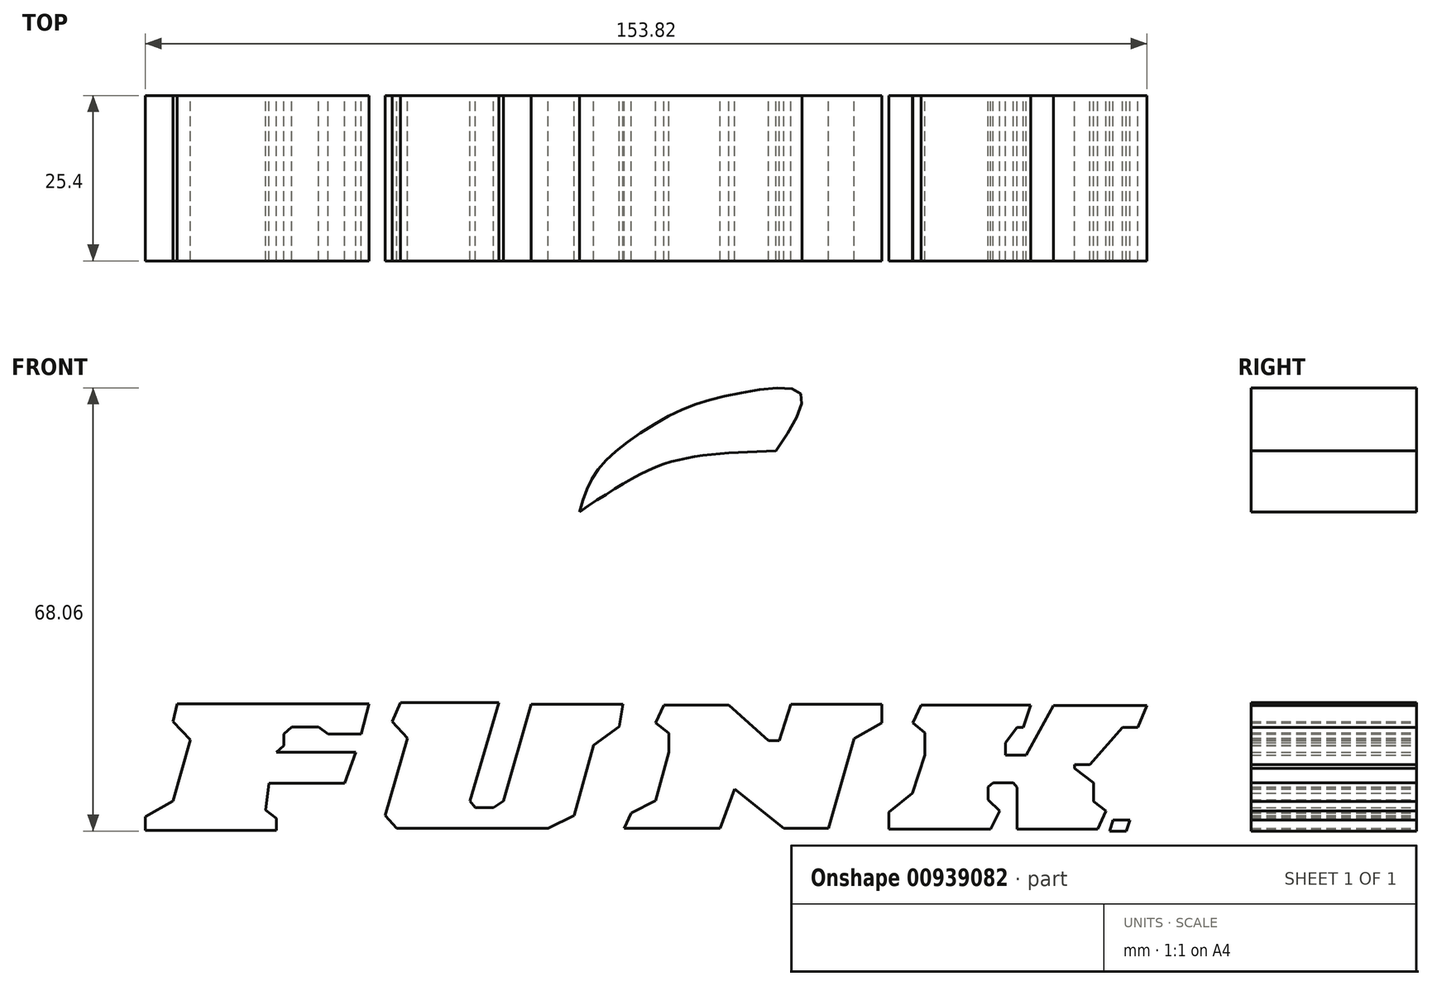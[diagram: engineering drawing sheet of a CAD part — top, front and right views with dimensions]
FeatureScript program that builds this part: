
annotation { "Feature Type Name" : "Feature", "Feature Type Description" : "" }
export const myFeature = defineFeature(function(context is Context, id is Id, definition is map)
    precondition{}
    {
        {
            var Q0;
            Q0=qCreatedBy(makeId("Front.planeOp"),FACE);
            var sketch = newSketch(context, id + "F0", { "sketchPlane" : qUnion([Q0])});
            skLineSegment(sketch, "E0", {"start": v(-70.91, 28.57) * mm, "end": v(-71.55, 25.87) * mm});
            skLineSegment(sketch, "E1", {"start": v(-71.55, 25.87) * mm, "end": v(-68.85, 23.1) * mm});
            skLineSegment(sketch, "E2", {"start": v(-68.85, 23.1) * mm, "end": v(-71.55, 13.7) * mm});
            skLineSegment(sketch, "E3", {"start": v(-71.55, 13.7) * mm, "end": v(-75.78, 11.28) * mm});
            skLineSegment(sketch, "E4", {"start": v(-75.78, 11.28) * mm, "end": v(-75.78, 9.14) * mm});
            skLineSegment(sketch, "E5", {"start": v(-75.78, 9.14) * mm, "end": v(-55.68, 9.14) * mm});
            skLineSegment(sketch, "E6", {"start": v(-55.68, 9.14) * mm, "end": v(-55.68, 11) * mm});
            skLineSegment(sketch, "E7", {"start": v(-55.68, 11) * mm, "end": v(-57.32, 12.28) * mm});
            skLineSegment(sketch, "E8", {"start": v(-57.32, 12.28) * mm, "end": v(-56.82, 16.4) * mm});
            skLineSegment(sketch, "E9", {"start": v(-56.82, 16.4) * mm, "end": v(-45.15, 16.4) * mm});
            skLineSegment(sketch, "E10", {"start": v(-45.15, 16.4) * mm, "end": v(-43.44, 21.17) * mm});
            skLineSegment(sketch, "E11", {"start": v(-43.44, 21.17) * mm, "end": v(-55.68, 21.17) * mm});
            skLineSegment(sketch, "E12", {"start": v(-55.68, 21.17) * mm, "end": v(-54.54, 22.17) * mm});
            skLineSegment(sketch, "E13", {"start": v(-54.54, 22.17) * mm, "end": v(-54.54, 23.95) * mm});
            skLineSegment(sketch, "E14", {"start": v(-54.54, 23.95) * mm, "end": v(-53.33, 25.01) * mm});
            skLineSegment(sketch, "E15", {"start": v(-53.33, 25.01) * mm, "end": v(-49.2, 25.01) * mm});
            skLineSegment(sketch, "E16", {"start": v(-49.2, 25.01) * mm, "end": v(-47.71, 23.95) * mm});
            skLineSegment(sketch, "E17", {"start": v(-47.71, 23.95) * mm, "end": v(-42.66, 23.95) * mm});
            skLineSegment(sketch, "E18", {"start": v(-42.66, 23.95) * mm, "end": v(-41.45, 28.57) * mm});
            skLineSegment(sketch, "E19", {"start": v(-41.45, 28.57) * mm, "end": v(-70.91, 28.57) * mm});
            skLineSegment(sketch, "E20", {"start": v(-36.61, 28.79) * mm, "end": v(-37.9, 25.87) * mm});
            skLineSegment(sketch, "E21", {"start": v(-37.9, 25.87) * mm, "end": v(-35.54, 23.3) * mm});
            skLineSegment(sketch, "E22", {"start": v(-35.54, 23.3) * mm, "end": v(-38.96, 11.42) * mm});
            skLineSegment(sketch, "E23", {"start": v(-38.96, 11.42) * mm, "end": v(-37.18, 9.5) * mm});
            skLineSegment(sketch, "E24", {"start": v(-37.18, 9.5) * mm, "end": v(-13.9, 9.5) * mm});
            skLineSegment(sketch, "E25", {"start": v(-13.9, 9.5) * mm, "end": v(-9.92, 11.42) * mm});
            skLineSegment(sketch, "E26", {"start": v(-9.92, 11.42) * mm, "end": v(-6.94, 22.24) * mm});
            skLineSegment(sketch, "E27", {"start": v(-6.94, 22.24) * mm, "end": v(-3.02, 25.09) * mm});
            skLineSegment(sketch, "E28", {"start": v(-3.02, 25.09) * mm, "end": v(-2.45, 28.5) * mm});
            skLineSegment(sketch, "E29", {"start": v(-2.45, 28.5) * mm, "end": v(-16.54, 28.5) * mm});
            skLineSegment(sketch, "E30", {"start": v(-16.54, 28.5) * mm, "end": v(-20.81, 13.7) * mm});
            skLineSegment(sketch, "E31", {"start": v(-20.81, 13.7) * mm, "end": v(-22.3, 12.63) * mm});
            skLineSegment(sketch, "E32", {"start": v(-22.3, 12.63) * mm, "end": v(-25.08, 12.63) * mm});
            skLineSegment(sketch, "E33", {"start": v(-25.08, 12.63) * mm, "end": v(-25.94, 13.7) * mm});
            skLineSegment(sketch, "E34", {"start": v(-25.94, 13.7) * mm, "end": v(-21.52, 28.79) * mm});
            skLineSegment(sketch, "E35", {"start": v(-21.52, 28.79) * mm, "end": v(-36.61, 28.79) * mm});
            skLineSegment(sketch, "E36", {"start": v(3.84, 28.43) * mm, "end": v(2.58, 25.66) * mm});
            skLineSegment(sketch, "E37", {"start": v(2.58, 25.66) * mm, "end": v(4.6, 24.05) * mm});
            skLineSegment(sketch, "E38", {"start": v(4.6, 24.05) * mm, "end": v(4.6, 21.13) * mm});
            skLineSegment(sketch, "E39", {"start": v(4.6, 21.13) * mm, "end": v(2.58, 13.74) * mm});
            skLineSegment(sketch, "E40", {"start": v(2.58, 13.74) * mm, "end": v(-1.2, 11.83) * mm});
            skLineSegment(sketch, "E41", {"start": v(-1.2, 11.83) * mm, "end": v(-2.25, 9.5) * mm});
            skLineSegment(sketch, "E42", {"start": v(-2.25, 9.5) * mm, "end": v(12.5, 9.5) * mm});
            skLineSegment(sketch, "E43", {"start": v(12.5, 9.5) * mm, "end": v(14.71, 15.5) * mm});
            skLineSegment(sketch, "E44", {"start": v(14.71, 15.5) * mm, "end": v(22.26, 9.5) * mm});
            skLineSegment(sketch, "E45", {"start": v(22.26, 9.5) * mm, "end": v(29.1, 9.5) * mm});
            skLineSegment(sketch, "E46", {"start": v(29.1, 9.5) * mm, "end": v(33.08, 23.25) * mm});
            skLineSegment(sketch, "E47", {"start": v(33.08, 23.25) * mm, "end": v(37.3, 25.66) * mm});
            skLineSegment(sketch, "E48", {"start": v(37.3, 25.66) * mm, "end": v(37.3, 28.5) * mm});
            skLineSegment(sketch, "E49", {"start": v(37.3, 28.5) * mm, "end": v(23.32, 28.5) * mm});
            skLineSegment(sketch, "E50", {"start": v(23.32, 28.5) * mm, "end": v(21.54, 22.95) * mm});
            skLineSegment(sketch, "E51", {"start": v(21.54, 22.95) * mm, "end": v(19.89, 22.95) * mm});
            skLineSegment(sketch, "E52", {"start": v(19.89, 22.95) * mm, "end": v(13.83, 28.43) * mm});
            skLineSegment(sketch, "E53", {"start": v(13.83, 28.43) * mm, "end": v(3.84, 28.43) * mm});
            skLineSegment(sketch, "E54", {"start": v(43.36, 28.43) * mm, "end": v(42.1, 25.66) * mm});
            skLineSegment(sketch, "E55", {"start": v(42.1, 25.66) * mm, "end": v(43.93, 24.16) * mm});
            skLineSegment(sketch, "E56", {"start": v(43.93, 24.16) * mm, "end": v(43.93, 20.74) * mm});
            skLineSegment(sketch, "E57", {"start": v(43.93, 20.74) * mm, "end": v(42, 14.9) * mm});
            skLineSegment(sketch, "E58", {"start": v(42, 14.9) * mm, "end": v(38.37, 11.99) * mm});
            skLineSegment(sketch, "E59", {"start": v(38.37, 11.99) * mm, "end": v(38.37, 9.35) * mm});
            skLineSegment(sketch, "E60", {"start": v(38.37, 9.35) * mm, "end": v(54.04, 9.35) * mm});
            skLineSegment(sketch, "E61", {"start": v(54.04, 9.35) * mm, "end": v(55.4, 12.13) * mm});
            skLineSegment(sketch, "E62", {"start": v(55.4, 12.13) * mm, "end": v(53.61, 13.84) * mm});
            skLineSegment(sketch, "E63", {"start": v(53.61, 13.84) * mm, "end": v(53.61, 14.98) * mm});
            skLineSegment(sketch, "E64", {"start": v(53.61, 14.98) * mm, "end": v(53.61, 15.83) * mm});
            skLineSegment(sketch, "E65", {"start": v(53.61, 15.83) * mm, "end": v(54.4, 16.47) * mm});
            skLineSegment(sketch, "E66", {"start": v(54.4, 16.47) * mm, "end": v(57.53, 16.47) * mm});
            skLineSegment(sketch, "E67", {"start": v(57.53, 16.47) * mm, "end": v(58.1, 15.76) * mm});
            skLineSegment(sketch, "E68", {"start": v(58.1, 15.76) * mm, "end": v(58.1, 9.35) * mm});
            skLineSegment(sketch, "E69", {"start": v(58.1, 9.35) * mm, "end": v(70.49, 9.35) * mm});
            skLineSegment(sketch, "E70", {"start": v(70.49, 9.35) * mm, "end": v(71.7, 12.13) * mm});
            skLineSegment(sketch, "E71", {"start": v(71.7, 12.13) * mm, "end": v(69.85, 13.62) * mm});
            skLineSegment(sketch, "E72", {"start": v(69.85, 13.62) * mm, "end": v(69.85, 16.47) * mm});
            skLineSegment(sketch, "E73", {"start": v(69.85, 16.47) * mm, "end": v(66.93, 18.68) * mm});
            skLineSegment(sketch, "E74", {"start": v(66.93, 18.68) * mm, "end": v(66.93, 19.25) * mm});
            skLineSegment(sketch, "E75", {"start": v(66.93, 19.25) * mm, "end": v(69.28, 19.25) * mm});
            skLineSegment(sketch, "E76", {"start": v(69.28, 19.25) * mm, "end": v(74.26, 24.95) * mm});
            skLineSegment(sketch, "E77", {"start": v(74.26, 24.95) * mm, "end": v(76.62, 24.95) * mm});
            skLineSegment(sketch, "E78", {"start": v(76.62, 24.95) * mm, "end": v(78.04, 28.36) * mm});
            skLineSegment(sketch, "E79", {"start": v(78.04, 28.36) * mm, "end": v(63.65, 28.36) * mm});
            skLineSegment(sketch, "E80", {"start": v(63.65, 28.36) * mm, "end": v(59.45, 20.74) * mm});
            skLineSegment(sketch, "E81", {"start": v(59.45, 20.74) * mm, "end": v(56.32, 20.74) * mm});
            skLineSegment(sketch, "E82", {"start": v(56.32, 20.74) * mm, "end": v(56.32, 22.6) * mm});
            skLineSegment(sketch, "E83", {"start": v(56.32, 22.6) * mm, "end": v(58.1, 24.95) * mm});
            skLineSegment(sketch, "E84", {"start": v(60.16, 28.43) * mm, "end": v(43.36, 28.43) * mm});
            skLineSegment(sketch, "E85", {"start": v(58.1, 24.95) * mm, "end": v(59.02, 24.95) * mm});
            skLineSegment(sketch, "E86", {"start": v(59.02, 24.95) * mm, "end": v(60.16, 28.43) * mm});
            skFitSpline(sketch, "E87", {"points": [v(-9.11, 58.08) * mm, v(-7.12, 63.35) * mm, v(-2.7, 68.05) * mm, v(6.27, 73.6) * mm, v(15.24, 76.29) * mm, v(24.78, 76.29) * mm, v(21.08, 67.48) * mm], "startDerivative": vector(11.73, 40.36) * mm, "endDerivative": vector(-41.06, -62.04) * mm});
            skFitSpline(sketch, "E88", {"points": [v(-9.11, 58.08) * mm, v(1.86, 64.63) * mm, v(10.12, 66.77) * mm, v(21.08, 67.48) * mm], "startDerivative": vector(31.1, 20.77) * mm, "endDerivative": vector(33.92, 1.37) * mm});
            skLineSegment(sketch, "E89", {"start": v(72.82, 10.75) * mm, "end": v(72.32, 9.06) * mm});
            skLineSegment(sketch, "E90", {"start": v(72.32, 9.06) * mm, "end": v(74.84, 9.06) * mm});
            skLineSegment(sketch, "E91", {"start": v(74.84, 9.06) * mm, "end": v(75.4, 10.75) * mm});
            skLineSegment(sketch, "E92", {"start": v(72.82, 10.75) * mm, "end": v(75.4, 10.75) * mm});
            skSolve(sketch);
        }
        {
            var Q0;
            Q0 = qSketchRegion(id + "F0", true);
            extrude(context, id + "F1", {"entities" : qUnion([Q0]), "depth" : 25.4 * mm, "offsetDistance" : 25.4 * mm});
        }
    });
